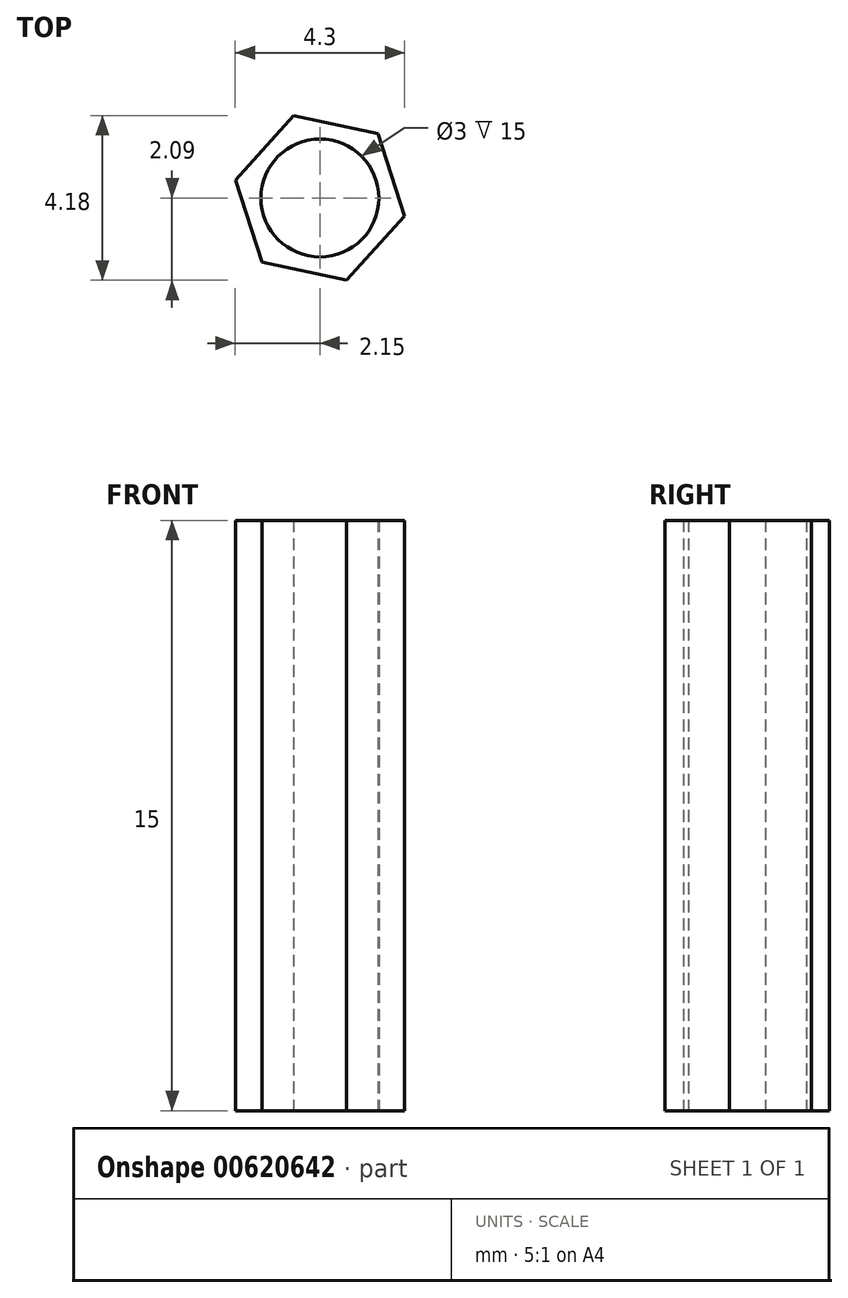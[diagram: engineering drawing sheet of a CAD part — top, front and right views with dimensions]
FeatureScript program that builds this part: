
annotation { "Feature Type Name" : "Feature", "Feature Type Description" : "" }
export const myFeature = defineFeature(function(context is Context, id is Id, definition is map)
    precondition{}
    {
        {
            var Q0;
            Q0=qCreatedBy(makeId("Top.planeOp"),FACE);
            var sketch = newSketch(context, id + "F0", { "sketchPlane" : qUnion([Q0])});
            skCircle(sketch, "E0.cCircle", {"center": v(0, 0) * mm, "radius": 1.9 * mm, "construction": true});
            skLineSegment(sketch, "E0.0", {"start": v(-2.15, 0.46) * mm, "end": v(-0.68, 2.09) * mm});
            skLineSegment(sketch, "E0.1", {"start": v(-0.68, 2.09) * mm, "end": v(1.47, 1.63) * mm});
            skLineSegment(sketch, "E0.2", {"start": v(1.47, 1.63) * mm, "end": v(2.15, -0.46) * mm});
            skLineSegment(sketch, "E0.3", {"start": v(2.15, -0.46) * mm, "end": v(0.68, -2.09) * mm});
            skLineSegment(sketch, "E0.4", {"start": v(0.68, -2.09) * mm, "end": v(-1.47, -1.63) * mm});
            skLineSegment(sketch, "E0.5", {"start": v(-1.47, -1.63) * mm, "end": v(-2.15, 0.46) * mm});
            skPoint(sketch, "E0.0.midPoint", {"position": v(-1.41, 1.27) * mm});
            skCircle(sketch, "E1", {"center": v(0, 0) * mm, "radius": 1.5 * mm});
            skSolve(sketch);
        }
        {
            var Q0;
            Q0 = qSketchRegion(id + "F0", true);
            extrude(context, id + "F1", {"entities" : qUnion([Q0]), "depth" : 15 * mm, "offsetDistance" : 25 * mm});
        }
    });
